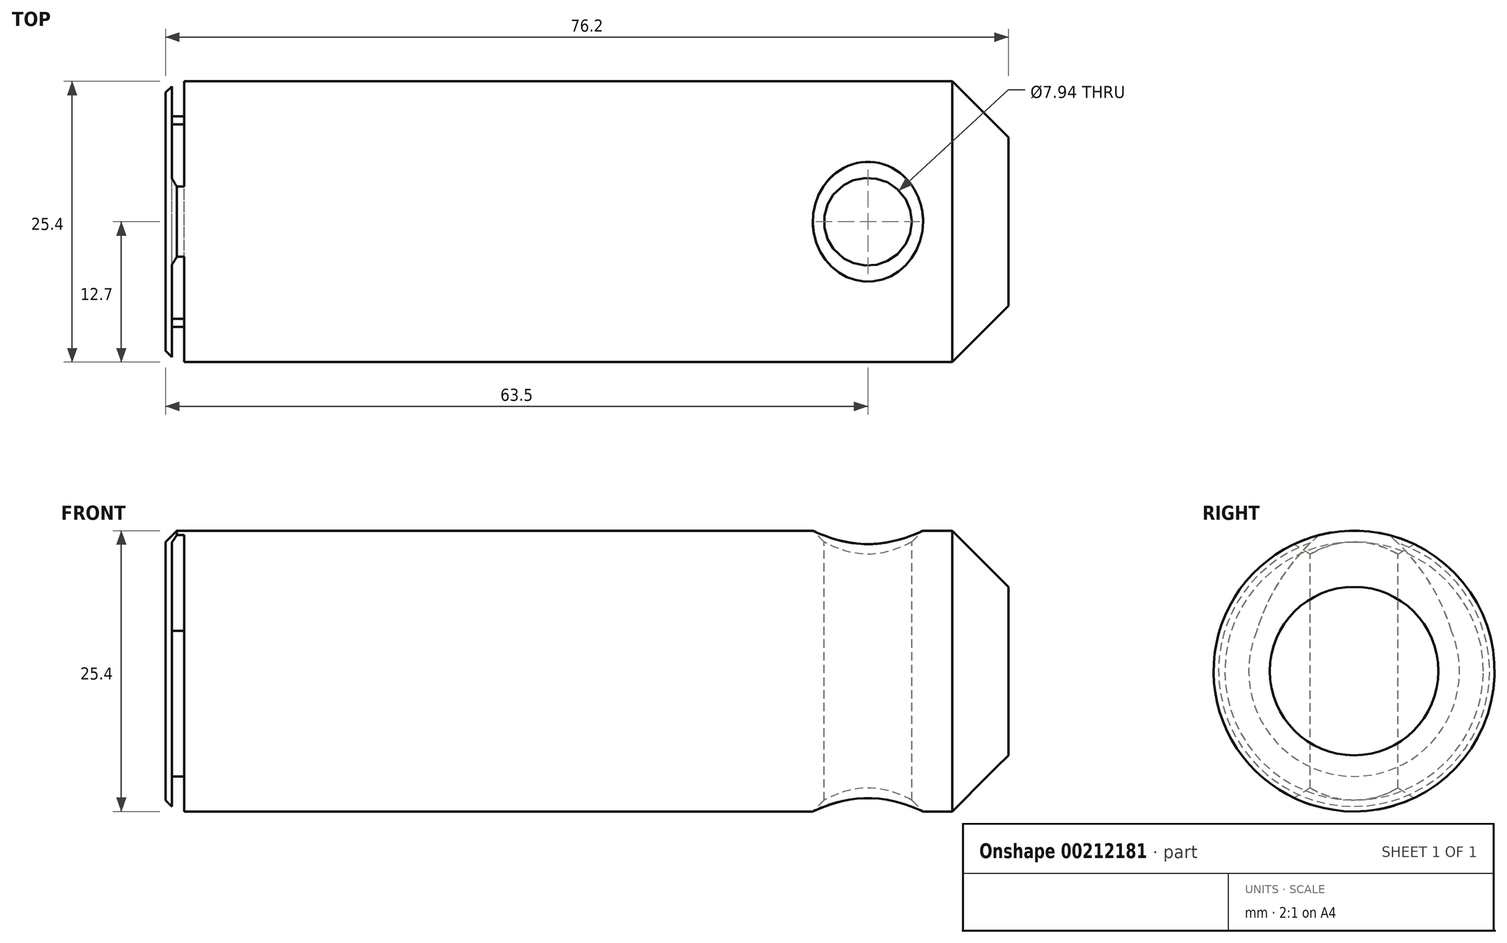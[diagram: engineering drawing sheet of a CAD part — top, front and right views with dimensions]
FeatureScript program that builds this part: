
annotation { "Feature Type Name" : "Feature", "Feature Type Description" : "" }
export const myFeature = defineFeature(function(context is Context, id is Id, definition is map)
    precondition{}
    {
        {
            var Q0;
            Q0=qCreatedBy(makeId("Right.planeOp"),FACE);
            var sketch = newSketch(context, id + "F0", { "sketchPlane" : qUnion([Q0])});
            skCircle(sketch, "E0", {"center": v(0, 0) * mm, "radius": 12.7 * mm});
            skCircle(sketch, "E1", {"center": v(0, 0) * mm, "radius": 9.53 * mm});
            skLineSegment(sketch, "E2", {"start": v(0, 0) * mm, "end": v(-8.8, 3.65) * mm, "construction": true});
            skLineSegment(sketch, "E3", {"start": v(0, 0) * mm, "end": v(0, 12.7) * mm, "construction": true});
            skLineSegment(sketch, "E4.0", {"start": v(3.18, 0) * mm, "end": v(3.18, 12.3) * mm, "construction": true});
            skLineSegment(sketch, "E5.0", {"start": v(-3.18, 0) * mm, "end": v(-3.18, 12.3) * mm, "construction": true});
            skLineSegment(sketch, "E6", {"start": v(0, 0) * mm, "end": v(8.8, 3.65) * mm, "construction": true});
            skArc(sketch, "E7", {"start": v(9.52, 0) * mm, "mid": v(7.53, 6.76) * mm, "end": v(3.18, 12.3) * mm});
            skArc(sketch, "E8", {"start": v(-3.18, 12.3) * mm, "mid": v(-7.53, 6.76) * mm, "end": v(-9.53, 0) * mm});
            skSolve(sketch);
        }
        {
            var Q0;
            Q0=makeQuery(id+"F0.imprint","IMPRINT",FACE,{"disambiguationData":[TD([[makeQuery(id+"F0.imprint","IMPRINT",EDGE,{"derivedFrom":sQuery(id+"F0.wireOp",EDGE,"E0")}),1.0]])]});
            var Q1;
            {var subQ0=sQuery(id+"F0.wireOp",EDGE,"E7");var subQ7=sQuery(id+"F0.wireOp",EDGE,"E0");var subQ8=makeQuery(id+"F0.imprint","INTERSECT",VERTEX,{"derivedFrom":[subQ7,subQ0]});Q1=makeQuery(id+"F0.imprint","IMPRINT",FACE,{"disambiguationData":[TD([[makeQuery(id+"F0.imprint","IMPRINT",EDGE,{"disambiguationData":[TD([[subQ8,1.0]])],"derivedFrom":subQ7}),1.0]])]});}
            var Q2;
            {var subQ0=sQuery(id+"F0.wireOp",EDGE,"E7");var subQ1=sQuery(id+"F0.wireOp",EDGE,"E1");var subQ2=makeQuery(id+"F0.imprint","INTERSECT",VERTEX,{"disambiguationData":[OD(1.0)],"derivedFrom":[subQ1,subQ0]});Q2=makeQuery(id+"F0.imprint","IMPRINT",FACE,{"disambiguationData":[TD([[makeQuery(id+"F0.imprint","IMPRINT",EDGE,{"disambiguationData":[TD([[subQ2,-1.0]])],"derivedFrom":subQ1}),1.0]])]});}
            var Q3;
            {var subQ0=sQuery(id+"F0.wireOp",EDGE,"E7");var subQ1=sQuery(id+"F0.wireOp",EDGE,"E1");var subQ2=makeQuery(id+"F0.imprint","INTERSECT",VERTEX,{"disambiguationData":[OD(0.0)],"derivedFrom":[subQ1,subQ0]});Q3=makeQuery(id+"F0.imprint","IMPRINT",FACE,{"disambiguationData":[TD([[makeQuery(id+"F0.imprint","IMPRINT",EDGE,{"disambiguationData":[TD([[subQ2,-1.0]])],"derivedFrom":subQ1}),1.0]])]});}
            var Q4;
            {var subQ0=sQuery(id+"F0.wireOp",EDGE,"E8");var subQ1=sQuery(id+"F0.wireOp",EDGE,"E1");var subQ2=makeQuery(id+"F0.imprint","INTERSECT",VERTEX,{"disambiguationData":[OD(0.0)],"derivedFrom":[subQ1,subQ0]});Q4=makeQuery(id+"F0.imprint","IMPRINT",FACE,{"disambiguationData":[TD([[makeQuery(id+"F0.imprint","IMPRINT",EDGE,{"disambiguationData":[TD([[subQ2,1.0]])],"derivedFrom":subQ1}),1.0]])]});}
            extrude(context, id + "F1", {"entities" : qUnion([Q0, Q1, Q2, Q3, Q4]), "depth" : 76.2 * mm});
        }
        {
            var Q0;
            {var subQ0=sQuery(id+"F0.wireOp",EDGE,"E7");var subQ7=sQuery(id+"F0.wireOp",EDGE,"E0");var subQ8=makeQuery(id+"F0.imprint","INTERSECT",VERTEX,{"derivedFrom":[subQ7,subQ0]});Q0=makeQuery(id+"F0.imprint","IMPRINT",FACE,{"disambiguationData":[TD([[makeQuery(id+"F0.imprint","IMPRINT",EDGE,{"disambiguationData":[TD([[subQ8,1.0]])],"derivedFrom":subQ7}),1.0]])]});}
            extrude(context, id + "F2", {"entities" : qUnion([Q0]), "operationType" : NewBodyOperationType.REMOVE, "depth" : ((1 + 1 / 8) + 9 / 16) * mm, "hasSecondDirection" : true, "secondDirectionOppositeDirection" : false, "secondDirectionDepth" : ((1 + 1 / 8) - 9 / 16) * mm});
        }
        {
            var Q0;
            Q0=qCreatedBy(makeId("Top.planeOp"),FACE);
            var sketch = newSketch(context, id + "F3", { "sketchPlane" : qUnion([Q0])});
            skCircle(sketch, "E9", {"center": v(63.5, 0) * mm, "radius": 3.97 * mm});
            skLineSegment(sketch, "E10", {"start": v(63.5, 0) * mm, "end": v(76.2, 0) * mm, "construction": true});
            skSolve(sketch);
        }
        {
            var Q0;
            Q0 = qSketchRegion(id + "F3", true);
            extrude(context, id + "F4", {"entities" : qUnion([Q0]), "operationType" : NewBodyOperationType.REMOVE, "endBound" : BoundingType.THROUGH_ALL, "oppositeDirection" : true, "depth" : 25.4 * mm, "hasSecondDirection" : true, "secondDirectionOppositeDirection" : false, "secondDirectionDepth" : 25.4 * mm});
        }
        {
            var Q0;
            Q0=makeQuery(id+"F1.opExtrude","CAP_EDGE",EDGE,{"disambiguationData":[OSD([sQuery(id+"F0.wireOp",EDGE,"E0")])],"isStart":false});
            chamfer(context, id + "F5", {"entities" : qUnion([Q0]), "width" : 5.08 * mm, "tangentPropagation" : true});
        }
        {
            var Q0;
            Q0=makeQuery(id+"F2.boolean.opBoolean","COPY",EDGE,{"derivedFrom":makeQuery(id+"F2.opExtrude","CAP_EDGE",EDGE,{"disambiguationData":[OSD([sQuery(id+"F0.wireOp",EDGE,"E0")])],"isStart":false})});
            var Q1;
            Q1=makeQuery(id+"F2.boolean.opBoolean","COPY",EDGE,{"derivedFrom":makeQuery(id+"F2.opExtrude","CAP_EDGE",EDGE,{"disambiguationData":[OSD([sQuery(id+"F0.wireOp",EDGE,"E0")])],"isStart":true})});
            var Q2;
            Q2=makeQuery(id+"F1.opExtrude","CAP_EDGE",EDGE,{"disambiguationData":[OSD([sQuery(id+"F0.wireOp",EDGE,"E0")])],"isStart":true});
            var Q3;
            Q3=makeQuery(id+"F2.boolean.opBoolean","COPY",EDGE,{"derivedFrom":makeQuery(id+"F2.opExtrude","SWEPT_EDGE",EDGE,{"disambiguationData":[OSD([sQuery(id+"F0.wireOp",EDGE,"E0"),sQuery(id+"F0.wireOp",EDGE,"E8")])]})});
            var Q4;
            Q4=makeQuery(id+"F2.boolean.opBoolean","COPY",EDGE,{"derivedFrom":makeQuery(id+"F2.opExtrude","SWEPT_EDGE",EDGE,{"disambiguationData":[OSD([sQuery(id+"F0.wireOp",EDGE,"E0"),sQuery(id+"F0.wireOp",EDGE,"E7")])]})});
            var Q5;
            Q5=makeQuery(id+"F4.boolean.opBoolean","COPY",FACE,{"derivedFrom":makeQuery(id+"F4.opExtrude","SWEPT_FACE",FACE,{"disambiguationData":[OSD([sQuery(id+"F3.wireOp",EDGE,"E9")])]})});
            chamfer(context, id + "F6", {"entities" : qUnion([Q0, Q1, Q2, Q3, Q4, Q5]), "width" : 1.02 * mm, "tangentPropagation" : true});
        }
    });
